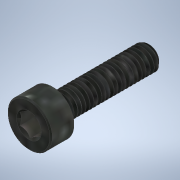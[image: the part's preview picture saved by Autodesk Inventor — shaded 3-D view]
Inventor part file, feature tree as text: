
AUTODESK INVENTOR PART (.ipt)
format: ipt  version: 2020.5 (Build 245400000, 400)  size: 637,952 bytes
history: native  units: in
note: dims shown in document units (in); Inventor stores cm internally (conversion verified against a paired STEP export)
features: revolve x1
ambient origin geometry x8: Origin, YZ Plane, XZ Plane, XY Plane, X Axis, Y Axis, Z Axis, Center Point
bodies: Solid1 (feature_tree)
feature tree (1):
  revolve  "Revolve2"  [1 undecoded]
note: 1 required parameter value undecoded (feature->parameter linkage not recoverable at this tier; creation-order binding heuristic only, values carry confidence <= 0.55)
